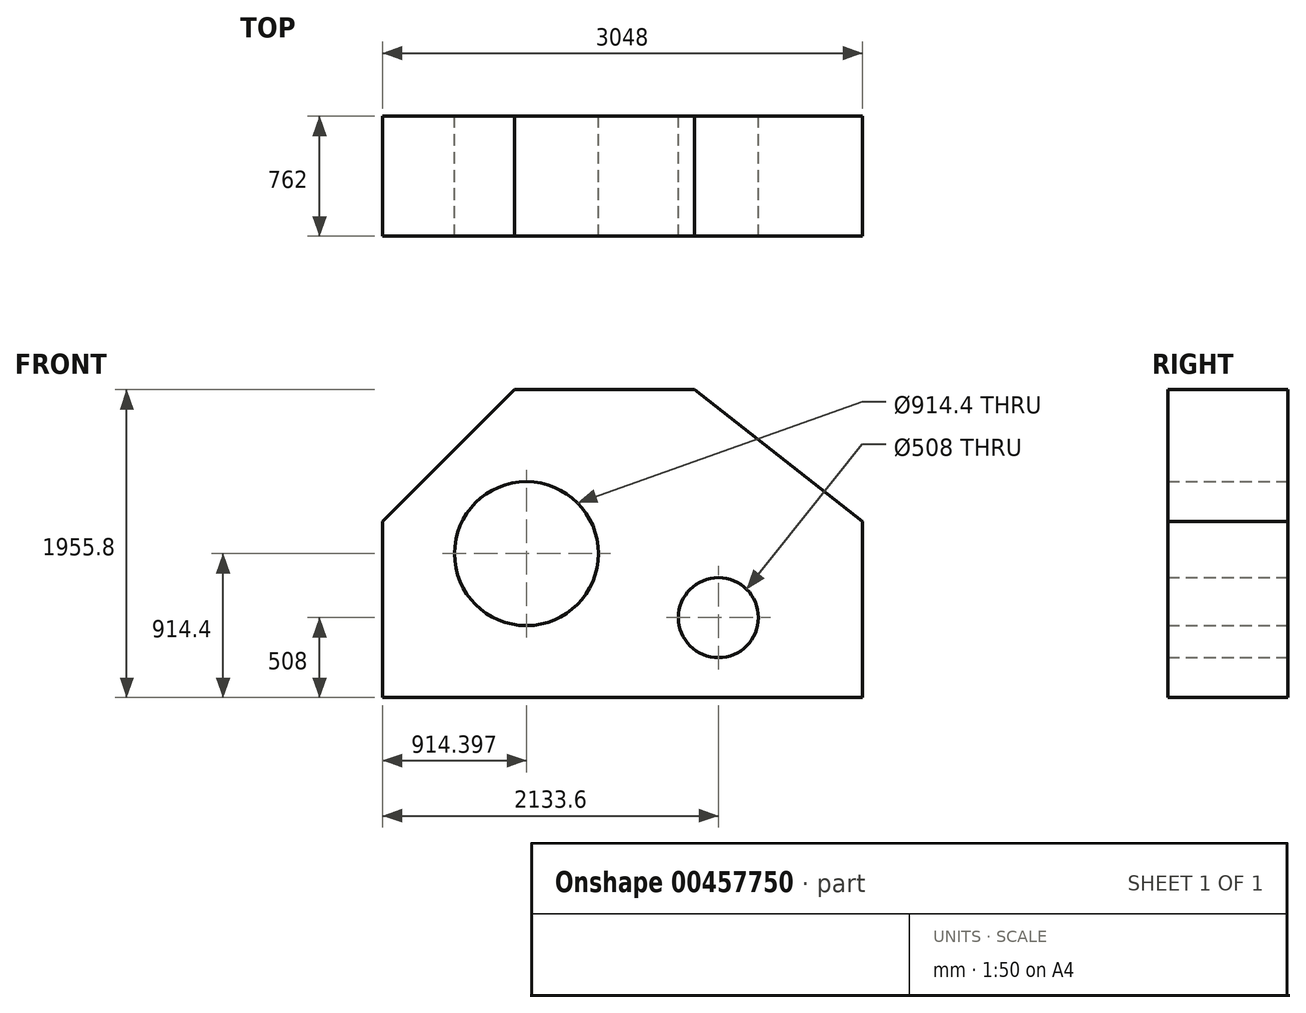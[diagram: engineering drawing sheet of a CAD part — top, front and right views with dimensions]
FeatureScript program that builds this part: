
annotation { "Feature Type Name" : "Feature", "Feature Type Description" : "" }
export const myFeature = defineFeature(function(context is Context, id is Id, definition is map)
    precondition{}
    {
        {
            var Q0;
            Q0=qCreatedBy(makeId("Front.planeOp"),FACE);
            var sketch = newSketch(context, id + "F0", { "sketchPlane" : qUnion([Q0])});
            skLineSegment(sketch, "E0", {"start": v(-751.21, 1041.4) * mm, "end": v(391.79, 1041.4) * mm});
            skLineSegment(sketch, "E1", {"start": v(391.79, 1041.4) * mm, "end": v(1458.59, 203.2) * mm});
            skLineSegment(sketch, "E2", {"start": v(1458.59, 203.2) * mm, "end": v(1458.59, -914.4) * mm});
            skLineSegment(sketch, "E3", {"start": v(1458.59, -914.4) * mm, "end": v(-1589.41, -914.4) * mm});
            skLineSegment(sketch, "E4", {"start": v(-1589.41, -914.4) * mm, "end": v(-1589.41, 203.2) * mm});
            skLineSegment(sketch, "E5", {"start": v(-1589.41, 203.2) * mm, "end": v(-751.21, 1041.4) * mm});
            skCircle(sketch, "E6", {"center": v(-675.01, 0) * mm, "radius": 457.2 * mm});
            skCircle(sketch, "E7", {"center": v(544.19, -406.4) * mm, "radius": 254 * mm});
            skSolve(sketch);
        }
        {
            var Q0;
            Q0=makeQuery(id+"F0.imprint","IMPRINT",FACE,{"disambiguationData":[TD([[makeQuery(id+"F0.imprint","IMPRINT",EDGE,{"derivedFrom":sQuery(id+"F0.wireOp",EDGE,"E0")}),-1.0]])]});
            extrude(context, id + "F1", {"entities" : qUnion([Q0]), "depth" : 762 * mm});
        }
    });
